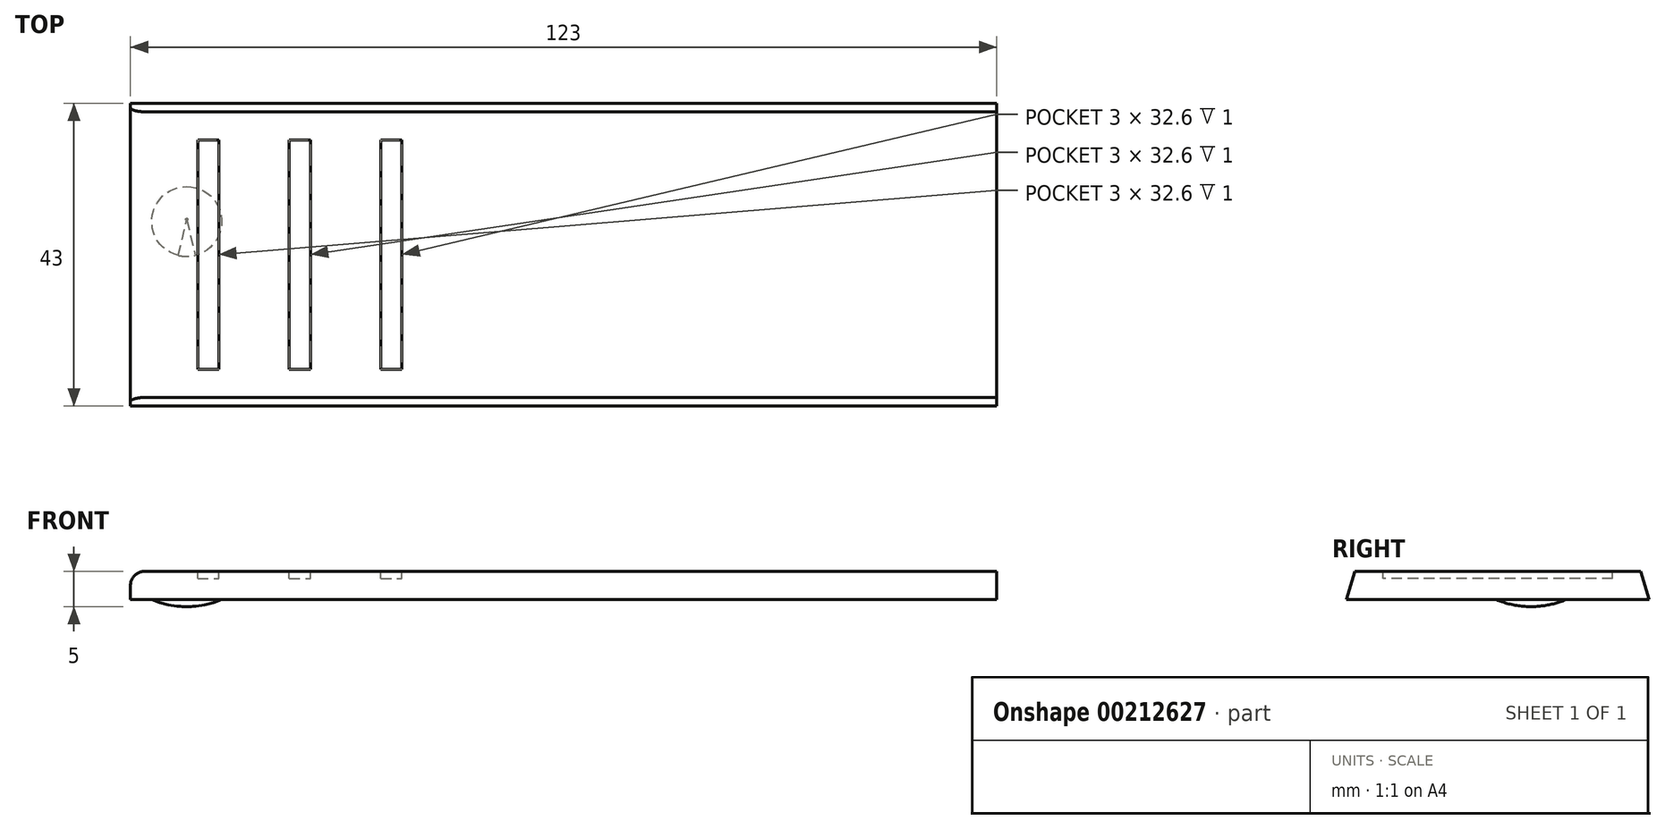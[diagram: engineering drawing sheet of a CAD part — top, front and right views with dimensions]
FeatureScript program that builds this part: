
annotation { "Feature Type Name" : "Feature", "Feature Type Description" : "" }
export const myFeature = defineFeature(function(context is Context, id is Id, definition is map)
    precondition{}
    {
        {
            var Q0;
            Q0=qCreatedBy(makeId("Right.planeOp"),FACE);
            var sketch = newSketch(context, id + "F0", { "sketchPlane" : qUnion([Q0])});
            skLineSegment(sketch, "E0", {"start": v(-15.37, 9.14) * mm, "end": v(25.23, 9.14) * mm});
            skLineSegment(sketch, "E1", {"start": v(25.23, 9.14) * mm, "end": v(26.43, 5.14) * mm});
            skLineSegment(sketch, "E2", {"start": v(26.43, 5.14) * mm, "end": v(-16.57, 5.14) * mm});
            skLineSegment(sketch, "E3", {"start": v(-16.57, 5.14) * mm, "end": v(-15.37, 9.14) * mm});
            skSolve(sketch);
        }
        {
            var Q0;
            Q0=makeQuery(id+"F0.imprint","IMPRINT",FACE,{"disambiguationData":[TD([[makeQuery(id+"F0.imprint","IMPRINT",EDGE,{"derivedFrom":sQuery(id+"F0.wireOp",EDGE,"E0")}),-1.0]])]});
            extrude(context, id + "F1", {"entities" : qUnion([Q0]), "depth" : 123 * mm, "offsetDistance" : 25 * mm});
        }
        {
            var Q0;
            Q0=makeQuery(id+"F1.opExtrude","SWEPT_FACE",FACE,{"disambiguationData":[OSD([sQuery(id+"F0.wireOp",EDGE,"E0")])]});
            var sketch = newSketch(context, id + "F2", { "sketchPlane" : qUnion([Q0])});
            skLineSegment(sketch, "E4.bottom", {"start": v(9.56, 21.23) * mm, "end": v(12.56, 21.23) * mm});
            skLineSegment(sketch, "E4.top", {"start": v(9.56, -11.37) * mm, "end": v(12.56, -11.37) * mm});
            skLineSegment(sketch, "E4.left", {"start": v(9.56, 21.23) * mm, "end": v(9.56, -11.37) * mm});
            skLineSegment(sketch, "E4.right", {"start": v(12.56, 21.23) * mm, "end": v(12.56, -11.37) * mm});
            skLineSegment(sketch, "E5.bottom", {"start": v(22.56, 21.23) * mm, "end": v(25.56, 21.23) * mm});
            skLineSegment(sketch, "E5.top", {"start": v(22.56, -11.37) * mm, "end": v(25.56, -11.37) * mm});
            skLineSegment(sketch, "E5.left", {"start": v(22.56, 21.23) * mm, "end": v(22.56, -11.37) * mm});
            skLineSegment(sketch, "E5.right", {"start": v(25.56, 21.23) * mm, "end": v(25.56, -11.37) * mm});
            skLineSegment(sketch, "E6.bottom", {"start": v(35.56, 21.23) * mm, "end": v(38.56, 21.23) * mm});
            skLineSegment(sketch, "E6.top", {"start": v(35.56, -11.37) * mm, "end": v(38.56, -11.37) * mm});
            skLineSegment(sketch, "E6.left", {"start": v(35.56, 21.23) * mm, "end": v(35.56, -11.37) * mm});
            skLineSegment(sketch, "E6.right", {"start": v(38.56, 21.23) * mm, "end": v(38.56, -11.37) * mm});
            skSolve(sketch);
        }
        {
            var Q0;
            Q0=makeQuery(id+"F2.imprint","IMPRINT",FACE,{"disambiguationData":[TD([[makeQuery(id+"F2.imprint","IMPRINT",EDGE,{"derivedFrom":sQuery(id+"F2.wireOp",EDGE,"E4.bottom")}),-1.0]])]});
            var Q1;
            Q1=makeQuery(id+"F2.imprint","IMPRINT",FACE,{"disambiguationData":[TD([[makeQuery(id+"F2.imprint","IMPRINT",EDGE,{"derivedFrom":sQuery(id+"F2.wireOp",EDGE,"E5.bottom")}),-1.0]])]});
            var Q2;
            Q2=makeQuery(id+"F2.imprint","IMPRINT",FACE,{"disambiguationData":[TD([[makeQuery(id+"F2.imprint","IMPRINT",EDGE,{"derivedFrom":sQuery(id+"F2.wireOp",EDGE,"E6.bottom")}),-1.0]])]});
            extrude(context, id + "F3", {"entities" : qUnion([Q0, Q1, Q2]), "operationType" : NewBodyOperationType.REMOVE, "oppositeDirection" : true, "depth" : 1 * mm});
        }
        {
            var Q0;
            Q0=makeQuery(id+"F1.opExtrude","SWEPT_FACE",FACE,{"disambiguationData":[OSD([sQuery(id+"F0.wireOp",EDGE,"E2")])]});
            var sketch = newSketch(context, id + "F4", { "sketchPlane" : qUnion([Q0])});
            skCircle(sketch, "E7", {"center": v(8, -9.93) * mm, "radius": 5.25 * mm});
            skSolve(sketch);
        }
        {
            var Q0;
            Q0=qCreatedBy(makeId("Right.planeOp"),FACE);
            cPlane(context, id + "F5", {"entities" : qUnion([Q0]), "cplaneType" : CPlaneType.OFFSET, "offset" : 8 * mm, "width" : 150 * mm, "height" : 150 * mm});
        }
        {
            var Q0;
            Q0=qCreatedBy(id+"F5.planeOp",FACE);
            var sketch = newSketch(context, id + "F6", { "sketchPlane" : qUnion([Q0])});
            skLineSegment(sketch, "E8", {"start": v(9.93, 5.14) * mm, "end": v(4.68, 5.14) * mm});
            skLineSegment(sketch, "E9", {"start": v(9.93, 5.14) * mm, "end": v(9.96, 4.14) * mm});
            skArc(sketch, "E10", {"start": v(4.68, 5.14) * mm, "mid": v(7.27, 4.37) * mm, "end": v(9.96, 4.14) * mm});
            skPoint(sketch, "E11.center.orphan", {"position": v(9.93, 5.14) * mm});
            skSolve(sketch);
        }
        {
            var Q0;
            Q0=makeQuery(id+"F6.imprint","IMPRINT",FACE,{"disambiguationData":[TD([[makeQuery(id+"F6.imprint","IMPRINT",EDGE,{"derivedFrom":sQuery(id+"F6.wireOp",EDGE,"E8")}),1.0]])]});
            var Q1;
            Q1=sQuery(id+"F6.wireOp",EDGE,"E9");
            revolve(context, id + "F7", {"operationType" : NewBodyOperationType.ADD, "entities" : qUnion([Q0]), "axis" : qUnion([Q1]), "revolveType" : RevolveType.FULL});
        }
        {
            var Q0;
            Q0=makeQuery(id+"F1.opExtrude","CAP_EDGE",EDGE,{"disambiguationData":[OSD([sQuery(id+"F0.wireOp",EDGE,"E0")])],"isStart":true});
            fillet(context, id + "F8", {"entities" : qUnion([Q0]), "radius" : 2 * mm, "tangentPropagation" : true, "allowEdgeOverflow" : false});
        }
    });
